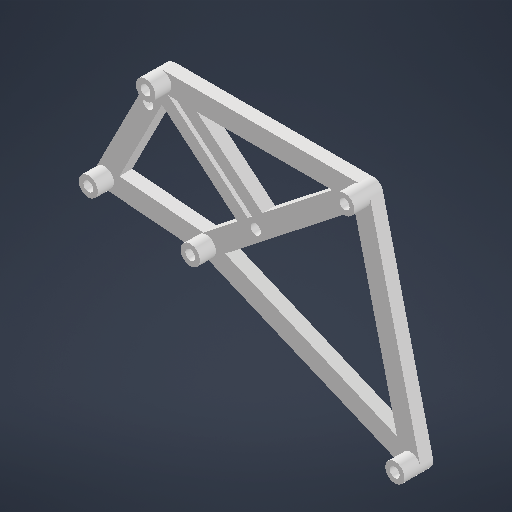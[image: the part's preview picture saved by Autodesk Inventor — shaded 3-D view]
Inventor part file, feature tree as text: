
AUTODESK INVENTOR PART (.ipt)
format: ipt  version: 2025 (Build 290162000, 162)  size: 335,360 bytes
history: native  units: mm
features: extrude x5, sketch x5, reference x5, other x2
ambient origin geometry x8: Origin, YZ Plane, XZ Plane, XY Plane, X Axis, Y Axis, Z Axis, Center Point
bodies: Solid1 (feature_tree)
feature tree (17):
  extrude  "Extrusion1"  Depth=6.0mm
  extrude  "Extrusion2"  Depth=6.0mm
  extrude  "Extrusion3"  Depth=6.0mm
  extrude  "Extrusion4"  Depth=6.0mm
  extrude  "Extrusion5"  Depth=6.0mm
  sketch  "Sketch1"  dims[d0=6.0mm d1=6.0mm]
  reference  "Reference1"
  reference  "Reference2"
  reference  "Reference3"
  reference  "Reference4"
  reference  "Reference5"
  sketch  "Sketch2"  dims[d2=6.0mm d3=6.0mm]
  sketch  "Sketch3"  dims[d4=6.0mm d5=6.0mm]
  sketch  "Sketch4"  dims[d6=6.0mm d7=6.0mm]
  sketch  "Sketch5"  dims[d8=6.0mm d9=6.0mm d10=6.0mm d11=4.0mm d12=0.0mm d18=10.0mm d19=0.0mm d21=0.05mm d22=0.05mm d23=0.05mm d24=0.05mm d25=0.05mm d26=4.0mm d27=0.0mm d28=3.1mm d29=3.1mm d30=3.1mm d31=3.1mm d32=3.1mm d36=6.981317mm d37=35.0mm d38=1.7mm d39=4.0mm d40=4.0mm d41=3.0mm d42=3.2mm d43=3.2mm d44=10.0mm d45=0.0mm d46=1.5mm d47=5.0mm d48=0.0mm]
  other  "Assembly1"
  other  "BTT E3 SKR MINI V3.0_3D:1"
